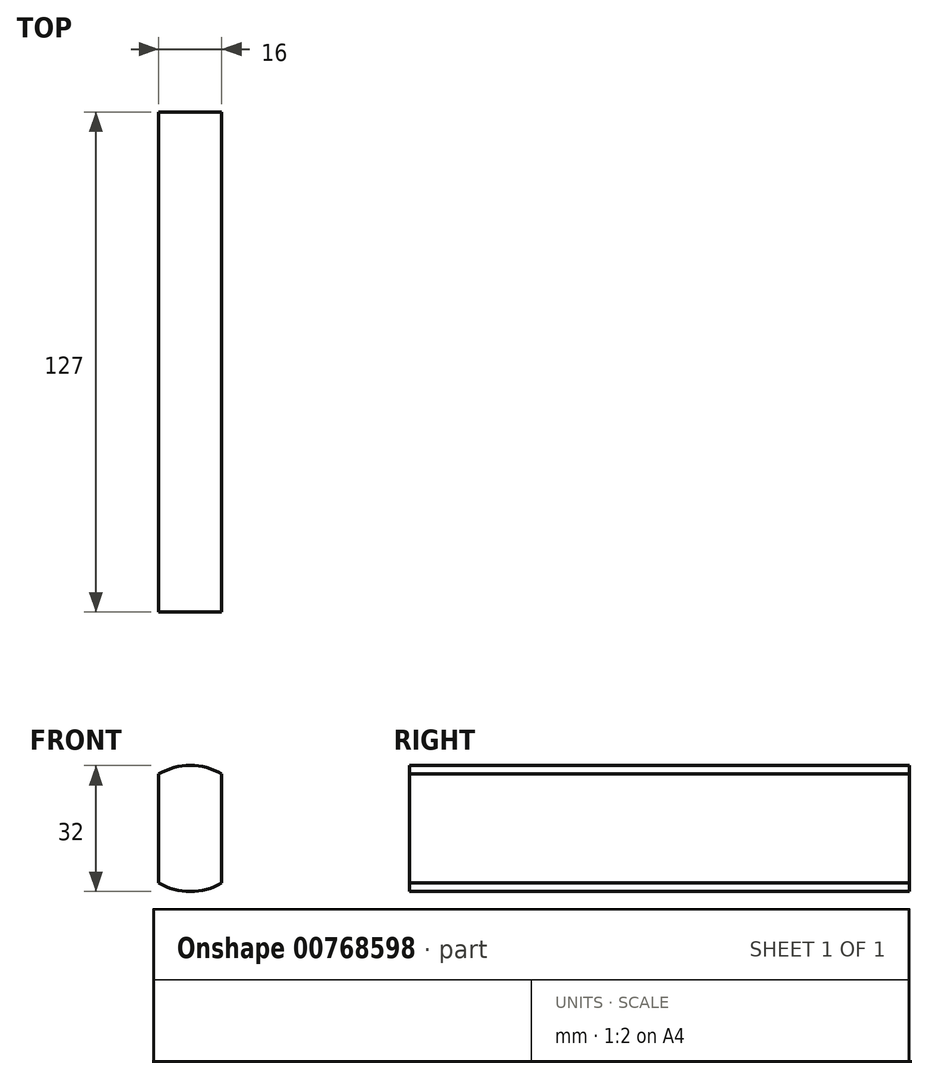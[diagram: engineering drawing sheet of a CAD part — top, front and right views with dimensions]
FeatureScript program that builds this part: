
annotation { "Feature Type Name" : "Feature", "Feature Type Description" : "" }
export const myFeature = defineFeature(function(context is Context, id is Id, definition is map)
    precondition{}
    {
        {
            var Q0;
            Q0=qCreatedBy(makeId("Front.planeOp"),FACE);
            var sketch = newSketch(context, id + "F0", { "sketchPlane" : qUnion([Q0])});
            skPoint(sketch, "E0", {"position": v(0, 16.07) * mm});
            skPoint(sketch, "E1", {"position": v(0, 15.97) * mm});
            skPoint(sketch, "E2", {"position": v(0, 16.17) * mm});
            skPoint(sketch, "E3", {"position": v(0, 16.02) * mm});
            skPoint(sketch, "E4", {"position": v(0, 16.12) * mm});
            skPoint(sketch, "E5", {"position": v(0, 16) * mm});
            skPoint(sketch, "E6", {"position": v(0, 15.98) * mm});
            skArc(sketch, "E7", {"start": v(8, 13.86) * mm, "mid": v(0, 16) * mm, "end": v(-8, 13.86) * mm});
            skLineSegment(sketch, "E8", {"start": v(8, 13.86) * mm, "end": v(8, -13.86) * mm});
            skPoint(sketch, "E8.startSnap0", {"position": v(8, 0) * mm});
            skLineSegment(sketch, "E9", {"start": v(-8, 13.86) * mm, "end": v(-8, -13.86) * mm});
            skPoint(sketch, "E9.startSnap0", {"position": v(-8, 0) * mm});
            skPoint(sketch, "E10.orphan", {"position": v(16, 0) * mm});
            skArc(sketch, "E11.trimOffspring", {"start": v(-8, -13.86) * mm, "mid": v(0, -16) * mm, "end": v(8, -13.86) * mm});
            skPoint(sketch, "E12.orphan", {"position": v(-16, 0) * mm});
            skSolve(sketch);
        }
        {
            var Q0;
            Q0 = qSketchRegion(id + "F0", true);
            extrude(context, id + "F1", {"entities" : qUnion([Q0]), "depth" : 127 * mm, "offsetDistance" : 25 * mm});
        }
    });
